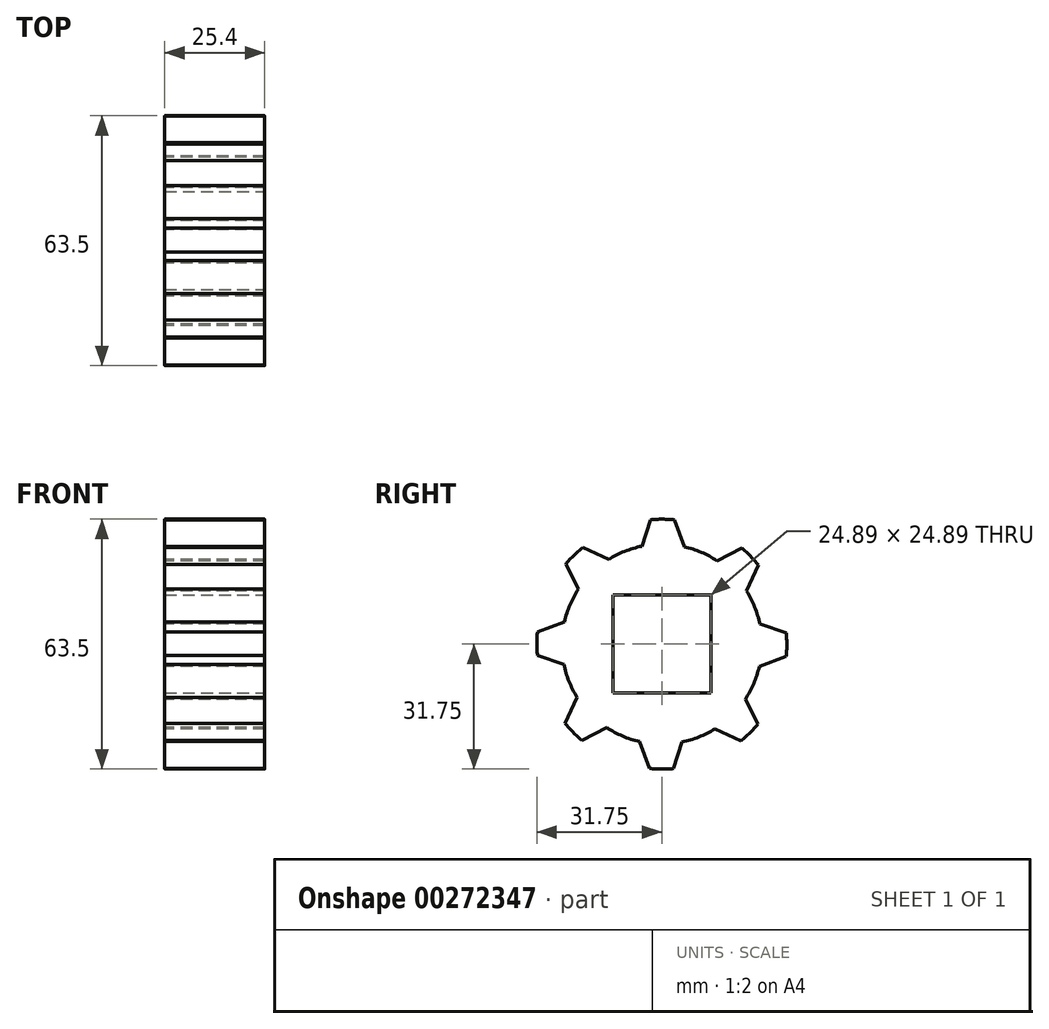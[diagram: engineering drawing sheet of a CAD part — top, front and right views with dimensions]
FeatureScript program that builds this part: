
annotation { "Feature Type Name" : "Feature", "Feature Type Description" : "" }
export const myFeature = defineFeature(function(context is Context, id is Id, definition is map)
    precondition{}
    {
        {
            var Q0;
            Q0=qCreatedBy(makeId("Right.planeOp"),FACE);
            var sketch = newSketch(context, id + "F0", { "sketchPlane" : qUnion([Q0])});
            skCircle(sketch, "E0", {"center": v(0, 0) * mm, "radius": 31.75 * mm});
            skCircle(sketch, "E1", {"center": v(0, 0) * mm, "radius": 25.4 * mm});
            skLineSegment(sketch, "E2", {"start": v(-2.9, 31.62) * mm, "end": v(-5.09, 24.89) * mm});
            skLineSegment(sketch, "E3", {"start": v(3.17, 31.6) * mm, "end": v(5.7, 24.75) * mm});
            skLineSegment(sketch, "E4.1.0", {"start": v(-24.4, 20.31) * mm, "end": v(-21.2, 14) * mm});
            skLineSegment(sketch, "E4.1.1", {"start": v(-20.1, 24.58) * mm, "end": v(-13.48, 21.53) * mm});
            skLineSegment(sketch, "E4.2.0", {"start": v(-31.62, -2.9) * mm, "end": v(-24.89, -5.09) * mm});
            skLineSegment(sketch, "E4.2.1", {"start": v(-31.6, 3.17) * mm, "end": v(-24.75, 5.7) * mm});
            skLineSegment(sketch, "E4.3.0", {"start": v(-20.31, -24.4) * mm, "end": v(-14, -21.2) * mm});
            skLineSegment(sketch, "E4.3.1", {"start": v(-24.58, -20.1) * mm, "end": v(-21.53, -13.48) * mm});
            skLineSegment(sketch, "E4.4.0", {"start": v(2.9, -31.62) * mm, "end": v(5.09, -24.89) * mm});
            skLineSegment(sketch, "E4.4.1", {"start": v(-3.17, -31.6) * mm, "end": v(-5.7, -24.75) * mm});
            skLineSegment(sketch, "E4.5.0", {"start": v(24.4, -20.31) * mm, "end": v(21.2, -14) * mm});
            skLineSegment(sketch, "E4.5.1", {"start": v(20.1, -24.58) * mm, "end": v(13.48, -21.53) * mm});
            skLineSegment(sketch, "E4.6.0", {"start": v(31.62, 2.9) * mm, "end": v(24.89, 5.09) * mm});
            skLineSegment(sketch, "E4.6.1", {"start": v(31.6, -3.17) * mm, "end": v(24.75, -5.7) * mm});
            skLineSegment(sketch, "E4.7.0", {"start": v(20.31, 24.4) * mm, "end": v(14, 21.2) * mm});
            skLineSegment(sketch, "E4.7.1", {"start": v(24.58, 20.1) * mm, "end": v(21.53, 13.48) * mm});
            skSolve(sketch);
        }
        {
            var Q0;
            {var subQ0=sQuery(id+"F0.wireOp",EDGE,"E1");var subQ8=makeQuery(id+"F0.imprint","INTERSECT",VERTEX,{"derivedFrom":[subQ0,sQuery(id+"F0.wireOp",EDGE,"E4.6.0")]});Q0=makeQuery(id+"F0.imprint","IMPRINT",FACE,{"disambiguationData":[TD([[makeQuery(id+"F0.imprint","IMPRINT",EDGE,{"disambiguationData":[TD([[subQ8,-1.0]])],"derivedFrom":subQ0}),1.0]])]});}
            var Q1;
            {var subQ0=sQuery(id+"F0.wireOp",EDGE,"E4.2.0");Q1=makeQuery(id+"F0.imprint","IMPRINT",FACE,{"disambiguationData":[TD([[makeQuery(id+"F0.imprint","IMPRINT",EDGE,{"derivedFrom":subQ0}),1.0]])]});}
            var Q2;
            {var subQ0=sQuery(id+"F0.wireOp",EDGE,"E4.1.0");Q2=makeQuery(id+"F0.imprint","IMPRINT",FACE,{"disambiguationData":[TD([[makeQuery(id+"F0.imprint","IMPRINT",EDGE,{"derivedFrom":subQ0}),1.0]])]});}
            var Q3;
            {var subQ0=sQuery(id+"F0.wireOp",EDGE,"E2");Q3=makeQuery(id+"F0.imprint","IMPRINT",FACE,{"disambiguationData":[TD([[makeQuery(id+"F0.imprint","IMPRINT",EDGE,{"derivedFrom":subQ0}),1.0]])]});}
            var Q4;
            {var subQ0=sQuery(id+"F0.wireOp",EDGE,"E4.7.0");Q4=makeQuery(id+"F0.imprint","IMPRINT",FACE,{"disambiguationData":[TD([[makeQuery(id+"F0.imprint","IMPRINT",EDGE,{"derivedFrom":subQ0}),1.0]])]});}
            var Q5;
            {var subQ0=sQuery(id+"F0.wireOp",EDGE,"E4.6.0");Q5=makeQuery(id+"F0.imprint","IMPRINT",FACE,{"disambiguationData":[TD([[makeQuery(id+"F0.imprint","IMPRINT",EDGE,{"derivedFrom":subQ0}),1.0]])]});}
            var Q6;
            {var subQ0=sQuery(id+"F0.wireOp",EDGE,"E4.5.0");Q6=makeQuery(id+"F0.imprint","IMPRINT",FACE,{"disambiguationData":[TD([[makeQuery(id+"F0.imprint","IMPRINT",EDGE,{"derivedFrom":subQ0}),1.0]])]});}
            var Q7;
            {var subQ0=sQuery(id+"F0.wireOp",EDGE,"E4.4.0");Q7=makeQuery(id+"F0.imprint","IMPRINT",FACE,{"disambiguationData":[TD([[makeQuery(id+"F0.imprint","IMPRINT",EDGE,{"derivedFrom":subQ0}),1.0]])]});}
            var Q8;
            {var subQ0=sQuery(id+"F0.wireOp",EDGE,"E4.3.0");Q8=makeQuery(id+"F0.imprint","IMPRINT",FACE,{"disambiguationData":[TD([[makeQuery(id+"F0.imprint","IMPRINT",EDGE,{"derivedFrom":subQ0}),1.0]])]});}
            extrude(context, id + "F1", {"entities" : qUnion([Q0, Q1, Q2, Q3, Q4, Q5, Q6, Q7, Q8]), "depth" : 25.4 * mm});
        }
        {
            var Q0;
            Q0=makeQuery(id+"F1.opExtrude","CAP_FACE",FACE,{"disambiguationData":[OSD([sQuery(id+"F0.wireOp",EDGE,"E0"),sQuery(id+"F0.wireOp",EDGE,"E1"),sQuery(id+"F0.wireOp",EDGE,"E2"),sQuery(id+"F0.wireOp",EDGE,"E3"),sQuery(id+"F0.wireOp",EDGE,"E4.1.0"),sQuery(id+"F0.wireOp",EDGE,"E4.1.1"),sQuery(id+"F0.wireOp",EDGE,"E4.2.0"),sQuery(id+"F0.wireOp",EDGE,"E4.2.1"),sQuery(id+"F0.wireOp",EDGE,"E4.3.0"),sQuery(id+"F0.wireOp",EDGE,"E4.3.1"),sQuery(id+"F0.wireOp",EDGE,"E4.4.0"),sQuery(id+"F0.wireOp",EDGE,"E4.4.1"),sQuery(id+"F0.wireOp",EDGE,"E4.5.0"),sQuery(id+"F0.wireOp",EDGE,"E4.5.1"),sQuery(id+"F0.wireOp",EDGE,"E4.6.0"),sQuery(id+"F0.wireOp",EDGE,"E4.6.1"),sQuery(id+"F0.wireOp",EDGE,"E4.7.0"),sQuery(id+"F0.wireOp",EDGE,"E4.7.1")])],"isStart":false});
            var sketch = newSketch(context, id + "F2", { "sketchPlane" : qUnion([Q0])});
            skLineSegment(sketch, "E5.bottom", {"start": v(-12.45, 12.45) * mm, "end": v(12.45, 12.45) * mm});
            skLineSegment(sketch, "E5.top", {"start": v(-12.45, -12.45) * mm, "end": v(12.45, -12.45) * mm});
            skLineSegment(sketch, "E5.left", {"start": v(-12.45, 12.45) * mm, "end": v(-12.45, -12.45) * mm});
            skLineSegment(sketch, "E5.right", {"start": v(12.45, 12.45) * mm, "end": v(12.45, -12.45) * mm});
            skSolve(sketch);
        }
        {
            var Q0;
            Q0=makeQuery(id+"F2.imprint","IMPRINT",FACE,{"disambiguationData":[TD([[makeQuery(id+"F2.imprint","IMPRINT",EDGE,{"derivedFrom":sQuery(id+"F2.wireOp",EDGE,"E5.bottom")}),-1.0]])]});
            extrude(context, id + "F3", {"entities" : qUnion([Q0]), "operationType" : NewBodyOperationType.REMOVE, "oppositeDirection" : true, "depth" : 25.4 * mm});
        }
    });
